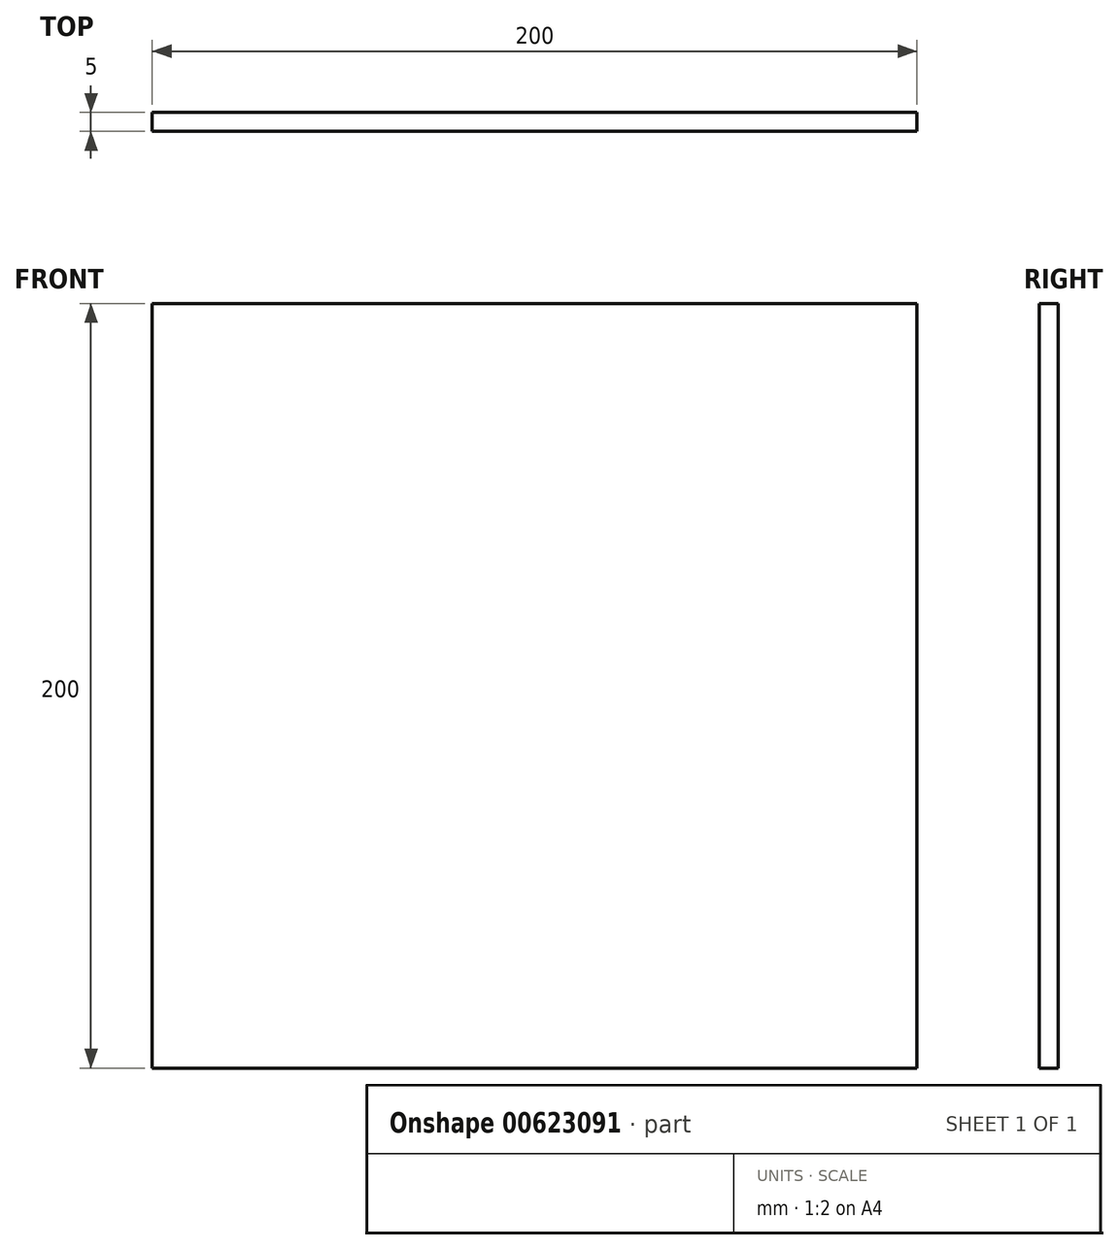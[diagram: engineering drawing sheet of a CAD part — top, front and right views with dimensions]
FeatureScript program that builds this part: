
annotation { "Feature Type Name" : "Feature", "Feature Type Description" : "" }
export const myFeature = defineFeature(function(context is Context, id is Id, definition is map)
    precondition{}
    {
        {
            var Q0;
            Q0=qCreatedBy(makeId("Front.planeOp"),FACE);
            var sketch = newSketch(context, id + "F0", { "sketchPlane" : qUnion([Q0])});
            skLineSegment(sketch, "E0.bottom", {"start": v(-200, 200) * mm, "end": v(0, 200) * mm});
            skLineSegment(sketch, "E0.top", {"start": v(-200, 0) * mm, "end": v(0, 0) * mm});
            skLineSegment(sketch, "E0.left", {"start": v(-200, 200) * mm, "end": v(-200, 0) * mm});
            skLineSegment(sketch, "E0.right", {"start": v(0, 200) * mm, "end": v(0, 0) * mm});
            skSolve(sketch);
        }
        {
            var Q0;
            Q0 = qSketchRegion(id + "F0", true);
            extrude(context, id + "F1", {"entities" : qUnion([Q0]), "depth" : 5 * mm, "offsetDistance" : 25 * mm});
        }
    });
